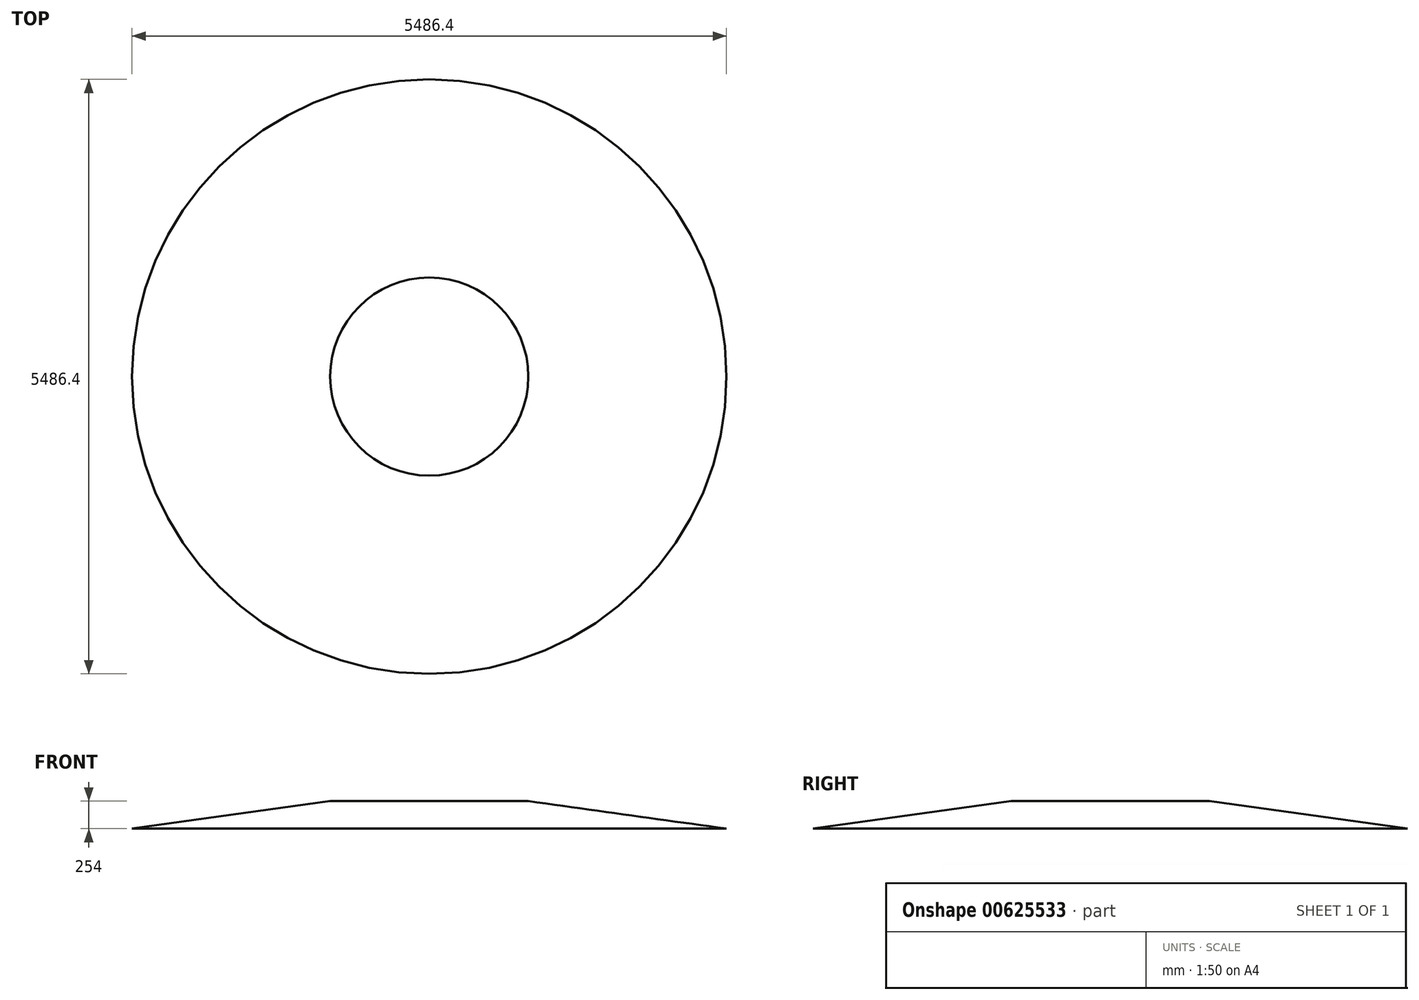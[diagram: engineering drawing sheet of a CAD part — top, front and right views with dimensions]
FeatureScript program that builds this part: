
annotation { "Feature Type Name" : "Feature", "Feature Type Description" : "" }
export const myFeature = defineFeature(function(context is Context, id is Id, definition is map)
    precondition{}
    {
        {
            var Q0;
            Q0=qCreatedBy(makeId("Front.planeOp"),FACE);
            var sketch = newSketch(context, id + "F0", { "sketchPlane" : qUnion([Q0])});
            skLineSegment(sketch, "E0", {"start": v(0, 0) * mm, "end": v(2743.2, 0) * mm});
            skLineSegment(sketch, "E1", {"start": v(2743.2, 0) * mm, "end": v(914.4, 254) * mm});
            skLineSegment(sketch, "E2", {"start": v(914.4, 254) * mm, "end": v(0, 254) * mm});
            skLineSegment(sketch, "E3", {"start": v(0, 254) * mm, "end": v(0, 0) * mm});
            skSolve(sketch);
        }
        {
            var Q0;
            Q0=makeQuery(id+"F0.imprint","IMPRINT",FACE,{"disambiguationData":[TD([[makeQuery(id+"F0.imprint","IMPRINT",EDGE,{"derivedFrom":sQuery(id+"F0.wireOp",EDGE,"E0")}),1.0]])]});
            var Q1;
            Q1=sQuery(id+"F0.wireOp",EDGE,"E3");
            revolve(context, id + "F1", {"entities" : qUnion([Q0]), "axis" : qUnion([Q1]), "revolveType" : RevolveType.FULL});
        }
    });
